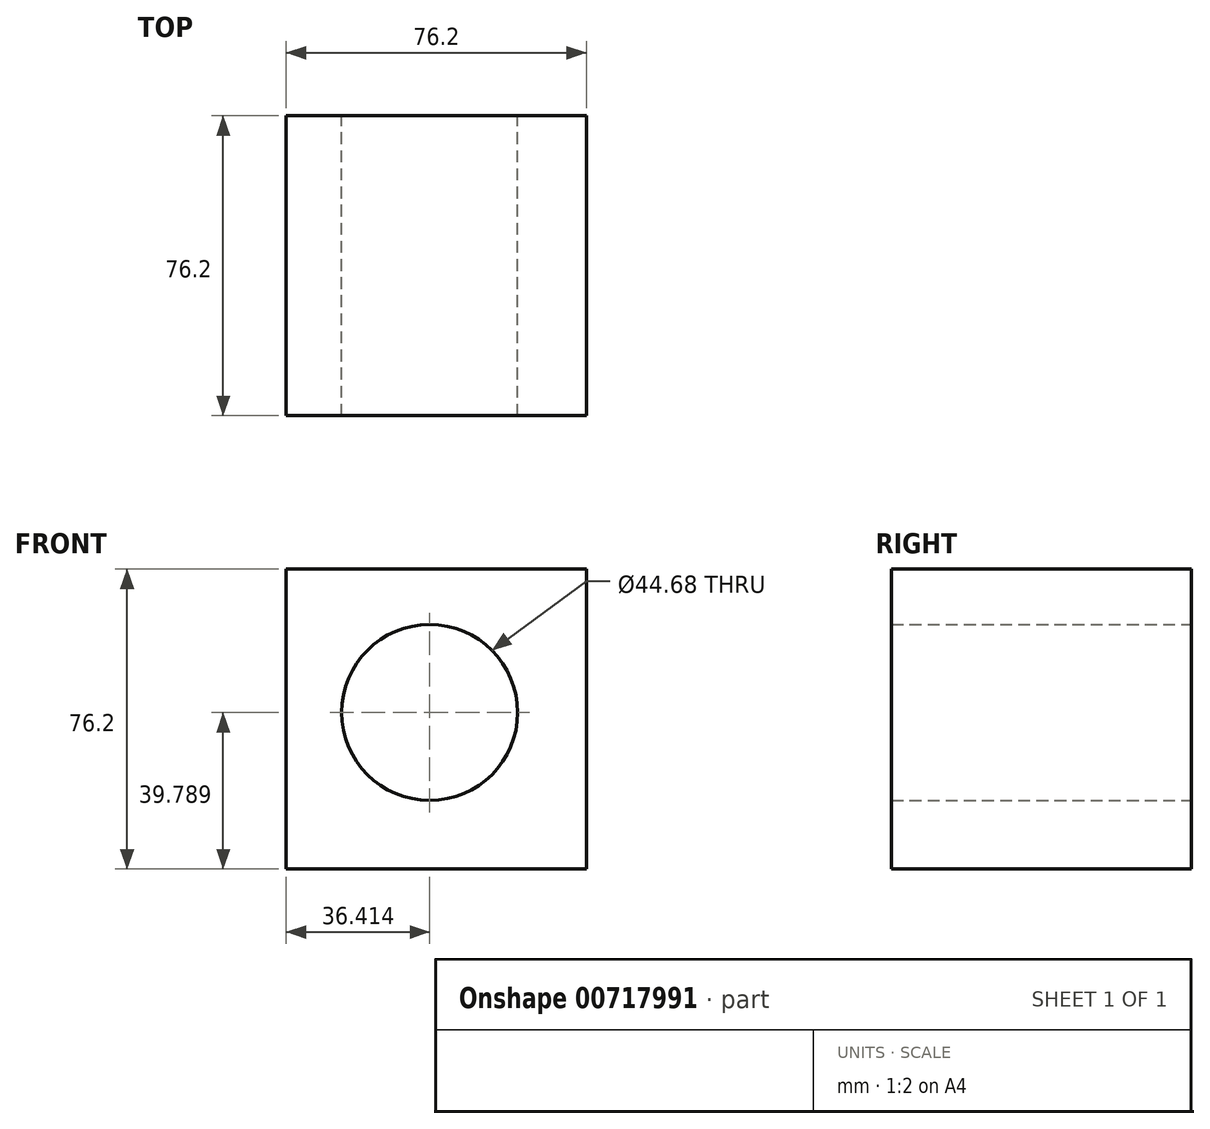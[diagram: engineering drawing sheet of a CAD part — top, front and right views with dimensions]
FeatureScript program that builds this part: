
annotation { "Feature Type Name" : "Feature", "Feature Type Description" : "" }
export const myFeature = defineFeature(function(context is Context, id is Id, definition is map)
    precondition{}
    {
        {
            var Q0;
            Q0=qCreatedBy(makeId("Front.planeOp"),FACE);
            var sketch = newSketch(context, id + "F0", { "sketchPlane" : qUnion([Q0])});
            skLineSegment(sketch, "E0.bottom", {"start": v(-40.3, 43.86) * mm, "end": v(35.9, 43.86) * mm});
            skLineSegment(sketch, "E0.top", {"start": v(-40.3, -32.34) * mm, "end": v(35.9, -32.34) * mm});
            skLineSegment(sketch, "E0.left", {"start": v(-40.3, 43.86) * mm, "end": v(-40.3, -32.34) * mm});
            skLineSegment(sketch, "E0.right", {"start": v(35.9, 43.86) * mm, "end": v(35.9, -32.34) * mm});
            skCircle(sketch, "E1", {"center": v(-3.9, 7.45) * mm, "radius": 22.34 * mm});
            skSolve(sketch);
        }
        {
            var Q0;
            Q0=makeQuery(id+"F0.imprint","IMPRINT",FACE,{"disambiguationData":[TD([[makeQuery(id+"F0.imprint","IMPRINT",EDGE,{"derivedFrom":sQuery(id+"F0.wireOp",EDGE,"E0.bottom")}),-1.0]])]});
            extrude(context, id + "F1", {"entities" : qUnion([Q0]), "depth" : 76.2 * mm, "offsetDistance" : 25.4 * mm});
        }
    });
